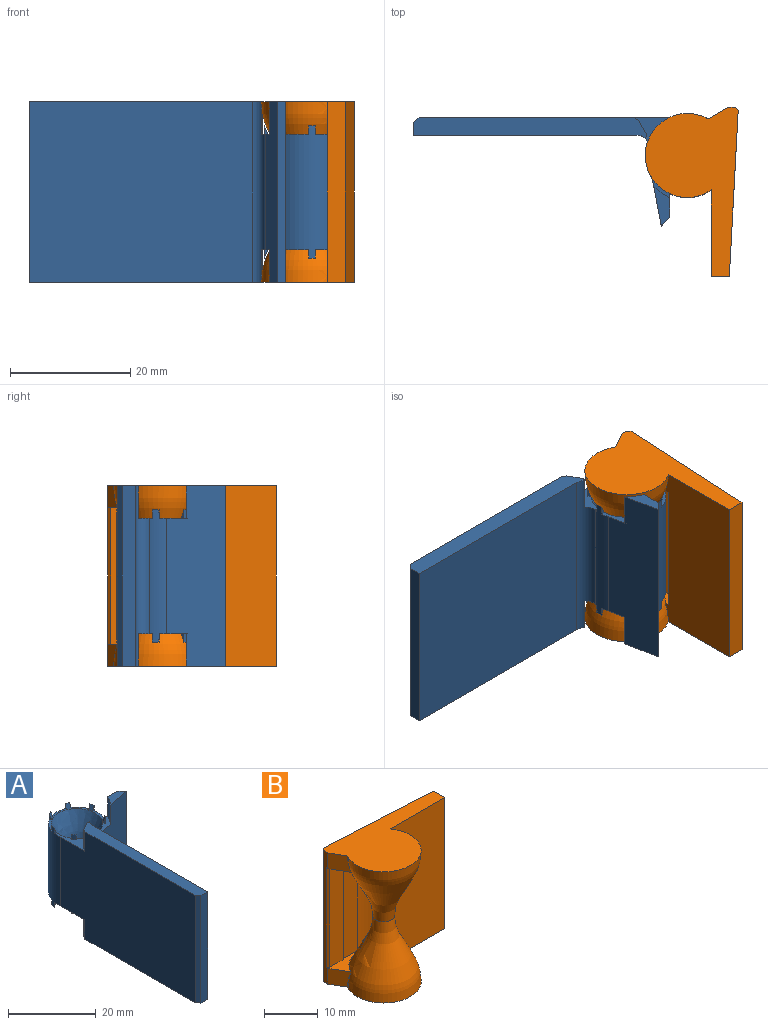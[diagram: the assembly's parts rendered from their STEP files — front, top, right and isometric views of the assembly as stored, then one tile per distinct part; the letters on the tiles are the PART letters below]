
ASSEMBLY  parts=2 mates=1
PART A: 80 faces, bbox 18.2x52x30 mm
  f0: cylinder r=6.5mm len=22mm, axis (0,0,1), area 60.3mm2, adj f6,f7,f10,f11,f12,f34,f46,f47
  f1: cylinder r=6.5mm len=22mm, axis (0,0,1), area 486.1mm2, adj f3,f4,f5,f6,f7,f16,f17,f18
  f2: cylinder r=6.5mm len=1.4mm, axis (0,0,1), area 1.6mm2, adj f7,f28,f29,f30
  f3: plane 3.78x3.17mm, normal (0,0,1), area 2.7mm2, adj f1,f8,f23,f27
  f4: plane 4.6x0.98mm, normal (0,0,1), area 2.7mm2, adj f1,f8,f20,f24
  f5: plane 3.78x3.17mm, normal (0,0,1), area 2.7mm2, adj f1,f8,f17,f21
  f6: plane 9.87x5.98mm, normal (0,0,1), area 17.6mm2, adj f0,f1,f8,f9,f11,f14,f15,f18
  f7: plane 7.36x6.5mm, normal (0,0,1), area 9.7mm2, adj f0,f1,f2,f8,f12,f26,f29,f30
  f8: revolved ~11.75x11.75mm, area 240.2mm2, adj f3,f4,f5,f6,f7,f10,f13,f16
  f9: cylinder r=6.5mm len=1.4mm, axis (0,0,1), area 1.6mm2, adj f6,f13,f14,f15
  f10: revolved ~1.4x1.13mm, area 1.6mm2, adj f0,f8,f11,f12
  f11: plane 1.4x0.6mm, normal (-1,0.09,0), area 0.4mm2, adj f0,f6,f10
  f12: plane 1.4x0.6mm, normal (1,0.09,0), area 0.4mm2, adj f0,f7,f10
  f13: revolved ~1.4x1.22mm, area 1.6mm2, adj f8,f9,f14,f15
  f14: plane 1.4x0.5mm, normal (-0.55,0.83,0), area 0.4mm2, adj f6,f9,f13
  f15: plane 1.4x0.43mm, normal (0.69,-0.72,0), area 0.4mm2, adj f6,f9,f13
  f16: revolved ~1.4x1.19mm, area 1.6mm2, adj f1,f8,f17,f18
  f17: plane 1.4x0.57mm, normal (0.31,0.95,0), area 0.4mm2, adj f1,f5,f16
  f18: plane 1.4x0.59mm, normal (-0.14,-0.99,0), area 0.4mm2, adj f1,f6,f16
  f19: revolved ~1.4x1.23mm, area 1.6mm2, adj f1,f8,f20,f21
  f20: plane 1.4x0.56mm, normal (0.94,0.35,0), area 0.4mm2, adj f1,f4,f19
  f21: plane 1.4x0.52mm, normal (-0.86,-0.51,0), area 0.4mm2, adj f1,f5,f19
  f22: revolved ~1.4x1.23mm, area 1.6mm2, adj f1,f8,f23,f24
  f23: plane 1.4x0.52mm, normal (0.86,-0.51,0), area 0.4mm2, adj f1,f3,f22
  f24: plane 1.4x0.56mm, normal (-0.94,0.35,0), area 0.4mm2, adj f1,f4,f22
  f25: revolved ~1.4x1.19mm, area 1.6mm2, adj f1,f8,f26,f27
  f26: plane 1.4x0.59mm, normal (0.14,-0.99,0), area 0.4mm2, adj f1,f7,f25
  f27: plane 1.4x0.57mm, normal (-0.31,0.95,0), area 0.4mm2, adj f1,f3,f25
  f28: revolved ~1.4x1.22mm, area 1.6mm2, adj f2,f8,f29,f30
  f29: plane 1.4x0.43mm, normal (-0.69,-0.72,0), area 0.4mm2, adj f2,f7,f28
  f30: plane 1.4x0.5mm, normal (0.55,0.83,0), area 0.4mm2, adj f2,f7,f28
  f31: plane 37.16x30mm, normal (1,0,0), area 1114.9mm2, adj f33,f37,f71,f79
  f32: plane 43.48x30mm, normal (-1,0,0), area 1220.4mm2, adj f1,f6,f37,f46,f71,f76,f77,f78
  f33: plane 30x2.13mm, normal (0,-1,0), area 64mm2, adj f31,f37,f71,f77
  f34: plane 30x9.82mm, normal (0.19,-0.98,0), area 264.2mm2, adj f0,f7,f36,f40,f41,f47,f74,f75
  f35: plane 30x4.5mm, normal (0,1,0), area 121.9mm2, adj f1,f7,f36,f40,f41,f47,f74,f75
  f36: plane 30x1.43mm, normal (0.71,0.7,0), area 60mm2, adj f34,f35,f41,f75
  f37: plane 38.77x3.52mm, normal (0,0,1), area 113.6mm2, adj f31,f32,f33,f38,f39,f77,f78,f79
  f38: plane 5.4x2.52mm, normal (-0.5,0.87,0), area 15.7mm2, adj f6,f37,f39,f78
  f39: cylinder r=7.6mm len=5.4mm, axis (0,0,1), area 3.4mm2, adj f6,f37,f38,f79
  f40: cylinder r=7.6mm len=5.4mm, axis (0,0,1), area 17.8mm2, adj f7,f34,f35,f41
  f41: plane 6.57x2.68mm, normal (0,0,1), area 9.6mm2, adj f34,f35,f36,f40
  f42: cylinder r=6.5mm len=1.4mm, axis (0,0,-1), area 1.6mm2, adj f47,f68,f69,f70
  f43: plane 3.78x3.17mm, normal (0,0,-1), area 2.7mm2, adj f1,f48,f63,f67
  f44: plane 4.6x0.98mm, normal (0,0,-1), area 2.7mm2, adj f1,f48,f60,f64
  f45: plane 3.78x3.17mm, normal (0,0,-1), area 2.7mm2, adj f1,f48,f57,f61
  f46: plane 9.87x5.98mm, normal (0,0,-1), area 17.6mm2, adj f0,f1,f32,f48,f49,f51,f54,f55
  f47: plane 7.36x6.5mm, normal (0,0,-1), area 9.7mm2, adj f0,f1,f34,f35,f42,f48,f52,f66
  f48: revolved ~11.75x11.75mm, area 240.2mm2, adj f8,f43,f44,f45,f46,f47,f50,f53
  f49: cylinder r=6.5mm len=1.4mm, axis (0,0,-1), area 1.6mm2, adj f46,f53,f54,f55
  f50: revolved ~1.4x1.13mm, area 1.6mm2, adj f0,f48,f51,f52
  f51: plane 1.4x0.6mm, normal (-1,0.09,0), area 0.4mm2, adj f0,f46,f50
  f52: plane 1.4x0.6mm, normal (1,0.09,0), area 0.4mm2, adj f0,f47,f50
  f53: revolved ~1.4x1.22mm, area 1.6mm2, adj f48,f49,f54,f55
  f54: plane 1.4x0.5mm, normal (-0.55,0.83,0), area 0.4mm2, adj f46,f49,f53
  f55: plane 1.4x0.43mm, normal (0.69,-0.72,0), area 0.4mm2, adj f46,f49,f53
  f56: revolved ~1.4x1.19mm, area 1.6mm2, adj f1,f48,f57,f58
  f57: plane 1.4x0.57mm, normal (0.31,0.95,0), area 0.4mm2, adj f1,f45,f56
  f58: plane 1.4x0.59mm, normal (-0.14,-0.99,0), area 0.4mm2, adj f1,f46,f56
  f59: revolved ~1.4x1.23mm, area 1.6mm2, adj f1,f48,f60,f61
  f60: plane 1.4x0.56mm, normal (0.94,0.35,0), area 0.4mm2, adj f1,f44,f59
  f61: plane 1.4x0.52mm, normal (-0.86,-0.51,0), area 0.4mm2, adj f1,f45,f59
  f62: revolved ~1.4x1.23mm, area 1.6mm2, adj f1,f48,f63,f64
  f63: plane 1.4x0.52mm, normal (0.86,-0.51,0), area 0.4mm2, adj f1,f43,f62
  f64: plane 1.4x0.56mm, normal (-0.94,0.35,0), area 0.4mm2, adj f1,f44,f62
  f65: revolved ~1.4x1.19mm, area 1.6mm2, adj f1,f48,f66,f67
  f66: plane 1.4x0.59mm, normal (0.14,-0.99,0), area 0.4mm2, adj f1,f47,f65
  f67: plane 1.4x0.57mm, normal (-0.31,0.95,0), area 0.4mm2, adj f1,f43,f65
  f68: revolved ~1.4x1.22mm, area 1.6mm2, adj f42,f48,f69,f70
  f69: plane 1.4x0.43mm, normal (-0.69,-0.72,0), area 0.4mm2, adj f42,f47,f68
  f70: plane 1.4x0.5mm, normal (0.55,0.83,0), area 0.4mm2, adj f42,f47,f68
  f71: plane 38.77x3.52mm, normal (0,0,-1), area 113.6mm2, adj f31,f32,f33,f72,f73,f76,f77,f79
  f72: plane 5.4x2.52mm, normal (-0.5,0.87,0), area 15.7mm2, adj f46,f71,f73,f76
  f73: cylinder r=7.6mm len=5.4mm, axis (0,0,-1), area 3.4mm2, adj f46,f71,f72,f79
  f74: cylinder r=7.6mm len=5.4mm, axis (0,0,-1), area 17.8mm2, adj f34,f35,f47,f75
  f75: plane 6.57x2.68mm, normal (0,0,-1), area 9.6mm2, adj f34,f35,f36,f74
  f76: plane 5.4x0.75mm, normal (-0.87,0.5,0), area 4.7mm2, adj f32,f46,f71,f72
  f77: plane 30x0.87mm, normal (-0.71,-0.71,0), area 36.7mm2, adj f32,f33,f37,f71
  f78: plane 5.4x0.75mm, normal (-0.87,0.5,0), area 4.7mm2, adj f6,f32,f37,f38
  f79: cylinder r=2mm len=30mm, axis (0,0,1), area 82.6mm2, adj f0,f6,f31,f37,f39,f46,f71,f73
PART B: 26 faces, bbox 28.3x15.7x30.2 mm
  f0: revolved ~15x13.96mm, area 404.8mm2, adj f1,f2,f3,f5,f6,f7,f11,f16
  f1: revolved ~3.23x0.59mm, area 0.5mm2, adj f0,f2,f4
  f2: plane 28.12x15.47mm, normal (0,0,1), area 233.1mm2, adj f0,f1,f3,f4,f8,f9,f10,f24
  f3: plane 30.21x15.21mm, normal (0,-1,0), area 433.1mm2, adj f0,f2,f6,f8,f11,f15,f16,f18
  f4: plane 4x3.79mm, normal (-0.87,-0.5,0), area 14.6mm2, adj f1,f2,f5,f10,f11
  f5: cylinder r=6.5mm len=5.8mm, axis (0,0,1), area 2.6mm2, adj f0,f4,f7,f11
  f6: plane 0.38x0.27mm, normal (-0.44,-0.9,0), area 0.1mm2, adj f0,f3,f11
  f7: plane 0.38x0.27mm, normal (-0.44,-0.9,0), area 0.1mm2, adj f0,f5,f11
  f8: plane 30x3mm, normal (1,0,0), area 90mm2, adj f2,f3,f9,f18
  f9: plane 30x27.59mm, normal (0.05,1,0), area 829mm2, adj f2,f8,f18,f24
  f10: plane 30x1.22mm, normal (-1,0,0), area 25.3mm2, adj f2,f4,f11,f18,f19,f23,f24,f25
  f11: plane 13.74x4.31mm, normal (0,0,-1), area 16.5mm2, adj f0,f3,f4,f5,f6,f7,f10,f12
  f12: plane 22.8x3.5mm, normal (0,-1,0), area 79.8mm2, adj f11,f13,f23,f25
  f13: plane 22.8x0.25mm, normal (1,0,0), area 5.7mm2, adj f11,f12,f14,f23
  f14: plane 22.8x4mm, normal (0,-1,0), area 91.2mm2, adj f11,f13,f15,f23
  f15: cylinder r=7mm len=22.8mm, axis (0,0,1), area 153.6mm2, adj f3,f11,f14,f23
  f16: revolved ~15x13.96mm, area 404.8mm2, adj f0,f3,f17,f18,f20,f21,f22,f23
  f17: revolved ~3.23x0.59mm, area 0.5mm2, adj f16,f18,f19
  f18: plane 28.12x15.47mm, normal (0,0,-1), area 233.1mm2, adj f3,f8,f9,f10,f16,f17,f19,f24
  f19: plane 4x3.79mm, normal (-0.87,-0.5,0), area 14.6mm2, adj f10,f17,f18,f20,f23
  f20: cylinder r=6.5mm len=5.8mm, axis (0,0,-1), area 2.6mm2, adj f16,f19,f22,f23
  f21: plane 0.38x0.27mm, normal (-0.44,-0.9,0), area 0.1mm2, adj f3,f16,f23
  f22: plane 0.38x0.27mm, normal (-0.44,-0.9,0), area 0.1mm2, adj f16,f20,f23
  f23: plane 13.74x4.31mm, normal (0,0,1), area 16.5mm2, adj f3,f10,f12,f13,f14,f15,f16,f19
  f24: plane 30x0.53mm, normal (-0.69,0.73,0), area 21.8mm2, adj f2,f9,f10,f18
  f25: plane 22.8x0.5mm, normal (-0.71,-0.71,0), area 16.1mm2, adj f10,f11,f12,f23
PLACE A rot(axis=(0,0,-1),90deg) t=(-7,20.12,-15)mm
PLACE B rot(axis=(0,0,-1),90deg) t=(-7,20.12,-15)mm
MATE revolute A.f0 <-> B.f15  axis (0,0,1) through (-7,20.12,-15)mm
